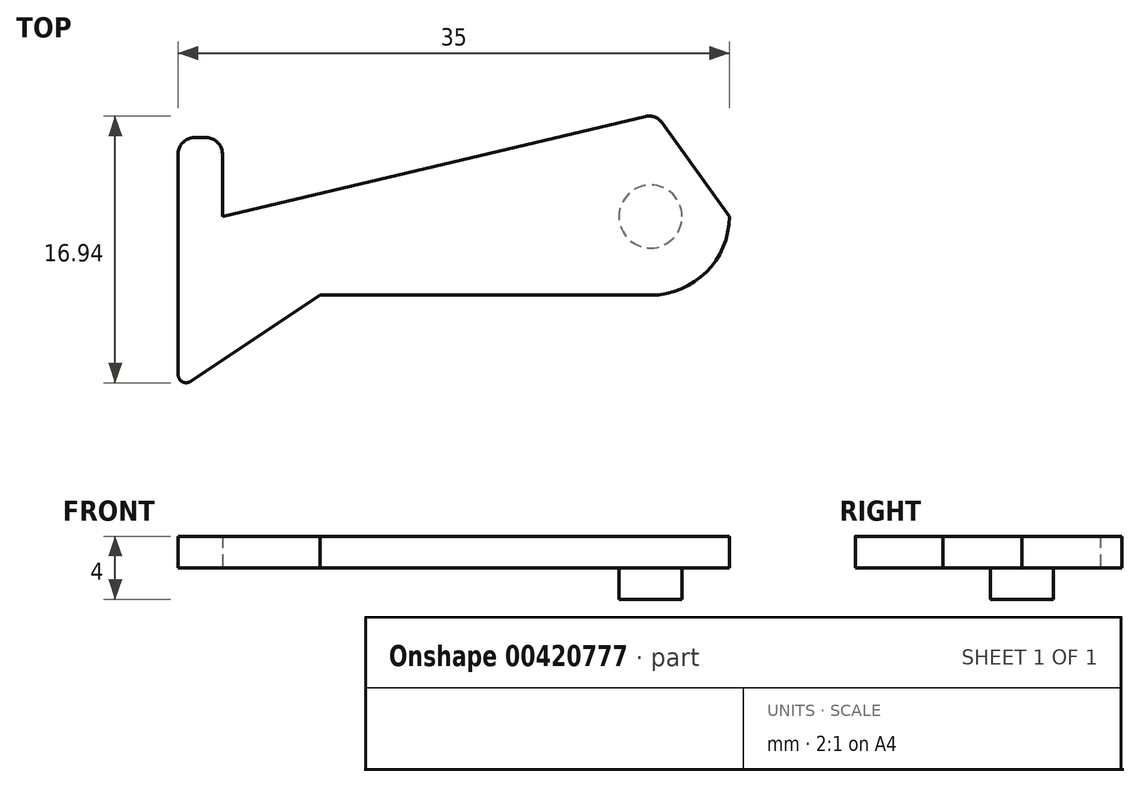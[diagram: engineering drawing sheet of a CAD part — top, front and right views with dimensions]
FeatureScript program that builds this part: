
annotation { "Feature Type Name" : "Feature", "Feature Type Description" : "" }
export const myFeature = defineFeature(function(context is Context, id is Id, definition is map)
    precondition{}
    {
        {
            var Q0;
            Q0=qCreatedBy(makeId("Top.planeOp"),FACE);
            var sketch = newSketch(context, id + "F0", { "sketchPlane" : qUnion([Q0])});
            skLineSegment(sketch, "E0.bottom", {"start": v(0, 0) * mm, "end": v(2.8, 0) * mm});
            skLineSegment(sketch, "E0.top", {"start": v(0, 5) * mm, "end": v(2.8, 5) * mm});
            skLineSegment(sketch, "E0.left", {"start": v(0, 0) * mm, "end": v(0, 5) * mm});
            skLineSegment(sketch, "E0.right", {"start": v(2.8, 0) * mm, "end": v(2.8, 5) * mm});
            skLineSegment(sketch, "E1.bottom", {"start": v(0, 0) * mm, "end": v(35, 0) * mm});
            skLineSegment(sketch, "E1.top", {"start": v(0, -5) * mm, "end": v(35, -5) * mm});
            skLineSegment(sketch, "E1.left", {"start": v(0, 0) * mm, "end": v(0, -5) * mm});
            skLineSegment(sketch, "E1.right", {"start": v(35, 0) * mm, "end": v(35, -5) * mm});
            skLineSegment(sketch, "E2", {"start": v(35, 0) * mm, "end": v(30.34, 6.5) * mm});
            skLineSegment(sketch, "E3", {"start": v(30.34, 6.5) * mm, "end": v(2.8, 0) * mm});
            skLineSegment(sketch, "E4", {"start": v(0, 0) * mm, "end": v(0, -11) * mm});
            skLineSegment(sketch, "E5", {"start": v(0, -11) * mm, "end": v(9, -5) * mm});
            skCircle(sketch, "E6", {"center": v(30, 0) * mm, "radius": 2 * mm});
            skSolve(sketch);
        }
        {
            var Q0;
            {var subQ0=sQuery(id+"F0.wireOp",EDGE,"E1.right");Q0=makeQuery(id+"F0.imprint","IMPRINT",FACE,{"disambiguationData":[TD([[makeQuery(id+"F0.imprint","IMPRINT",EDGE,{"derivedFrom":subQ0}),-1.0]])]});}
            var Q1;
            {var subQ3=sQuery(id+"F0.wireOp",EDGE,"E5");Q1=makeQuery(id+"F0.imprint","IMPRINT",FACE,{"disambiguationData":[TD([[makeQuery(id+"F0.imprint","IMPRINT",EDGE,{"derivedFrom":subQ3}),1.0]])]});}
            var Q2;
            {var subQ2=sQuery(id+"F0.wireOp",EDGE,"E2");Q2=makeQuery(id+"F0.imprint","IMPRINT",FACE,{"disambiguationData":[TD([[makeQuery(id+"F0.imprint","IMPRINT",EDGE,{"derivedFrom":subQ2}),1.0]])]});}
            var Q3;
            Q3=makeQuery(id+"F0.imprint","IMPRINT",FACE,{"disambiguationData":[TD([[makeQuery(id+"F0.imprint","IMPRINT",EDGE,{"derivedFrom":sQuery(id+"F0.wireOp",EDGE,"E0.top")}),-1.0]])]});
            var Q4;
            {var subQ0=sQuery(id+"F0.wireOp",EDGE,"E6");var subQ1=sQuery(id+"F0.wireOp",EDGE,"E1.bottom");var subQ2=makeQuery(id+"F0.imprint","INTERSECT",VERTEX,{"disambiguationData":[OD(0.0)],"derivedFrom":[subQ1,subQ0]});Q4=makeQuery(id+"F0.imprint","IMPRINT",FACE,{"disambiguationData":[TD([[makeQuery(id+"F0.imprint","IMPRINT",EDGE,{"disambiguationData":[TD([[subQ2,-1.0]])],"derivedFrom":subQ1}),1.0]])]});}
            var Q5;
            {var subQ0=sQuery(id+"F0.wireOp",EDGE,"E6");var subQ1=sQuery(id+"F0.wireOp",EDGE,"E1.bottom");var subQ2=makeQuery(id+"F0.imprint","INTERSECT",VERTEX,{"disambiguationData":[OD(0.0)],"derivedFrom":[subQ1,subQ0]});Q5=makeQuery(id+"F0.imprint","IMPRINT",FACE,{"disambiguationData":[TD([[makeQuery(id+"F0.imprint","IMPRINT",EDGE,{"disambiguationData":[TD([[subQ2,-1.0]])],"derivedFrom":subQ1}),-1.0]])]});}
            extrude(context, id + "F1", {"entities" : qUnion([Q0, Q1, Q2, Q3, Q4, Q5]), "depth" : 2 * mm});
        }
        {
            var Q0;
            {var subQ0=sQuery(id+"F0.wireOp",EDGE,"E6");var subQ1=sQuery(id+"F0.wireOp",EDGE,"E1.bottom");var subQ2=makeQuery(id+"F0.imprint","INTERSECT",VERTEX,{"disambiguationData":[OD(0.0)],"derivedFrom":[subQ1,subQ0]});Q0=makeQuery(id+"F0.imprint","IMPRINT",FACE,{"disambiguationData":[TD([[makeQuery(id+"F0.imprint","IMPRINT",EDGE,{"disambiguationData":[TD([[subQ2,-1.0]])],"derivedFrom":subQ1}),1.0]])]});}
            var Q1;
            {var subQ0=sQuery(id+"F0.wireOp",EDGE,"E6");var subQ1=sQuery(id+"F0.wireOp",EDGE,"E1.bottom");var subQ2=makeQuery(id+"F0.imprint","INTERSECT",VERTEX,{"disambiguationData":[OD(0.0)],"derivedFrom":[subQ1,subQ0]});Q1=makeQuery(id+"F0.imprint","IMPRINT",FACE,{"disambiguationData":[TD([[makeQuery(id+"F0.imprint","IMPRINT",EDGE,{"disambiguationData":[TD([[subQ2,-1.0]])],"derivedFrom":subQ1}),-1.0]])]});}
            var Q2;
            Q2=sQuery(id+"F0.wireOp",EDGE,"E6");
            extrude(context, id + "F2", {"entities" : qUnion([Q0, Q1]), "surfaceEntities" : qUnion([Q2]), "oppositeDirection" : true, "depth" : 2 * mm});
        }
        {
            var Q0;
            Q0=makeQuery(id+"F1.opExtrude","SWEPT_EDGE",EDGE,{"disambiguationData":[OSD([sQuery(id+"F0.wireOp",EDGE,"E1.top"),sQuery(id+"F0.wireOp",EDGE,"E1.right")])]});
            fillet(context, id + "F3", {"entities" : qUnion([Q0]), "radius" : 5 * mm, "tangentPropagation" : true, "allowEdgeOverflow" : false});
        }
        {
            var Q0;
            Q0=makeQuery(id+"F1.opExtrude","SWEPT_EDGE",EDGE,{"disambiguationData":[OSD([sQuery(id+"F0.wireOp",EDGE,"E0.top"),sQuery(id+"F0.wireOp",EDGE,"E0.left")])]});
            var Q1;
            Q1=makeQuery(id+"F1.opExtrude","SWEPT_EDGE",EDGE,{"disambiguationData":[OSD([sQuery(id+"F0.wireOp",EDGE,"E0.top"),sQuery(id+"F0.wireOp",EDGE,"E0.right")])]});
            fillet(context, id + "F4", {"entities" : qUnion([Q0, Q1]), "radius" : 1 * mm, "tangentPropagation" : true, "allowEdgeOverflow" : false});
        }
        {
            var Q0;
            Q0=makeQuery(id+"F1.opExtrude","SWEPT_EDGE",EDGE,{"disambiguationData":[OSD([sQuery(id+"F0.wireOp",EDGE,"E2"),sQuery(id+"F0.wireOp",EDGE,"E3")])]});
            fillet(context, id + "F5", {"entities" : qUnion([Q0]), "radius" : 1 * mm, "tangentPropagation" : true, "allowEdgeOverflow" : false});
        }
        {
            var Q0;
            Q0=makeQuery(id+"F1.opExtrude","SWEPT_EDGE",EDGE,{"disambiguationData":[OSD([sQuery(id+"F0.wireOp",EDGE,"E4"),sQuery(id+"F0.wireOp",EDGE,"E5")])]});
            fillet(context, id + "F6", {"entities" : qUnion([Q0]), "radius" : 0.5 * mm, "tangentPropagation" : true, "allowEdgeOverflow" : false});
        }
    });
